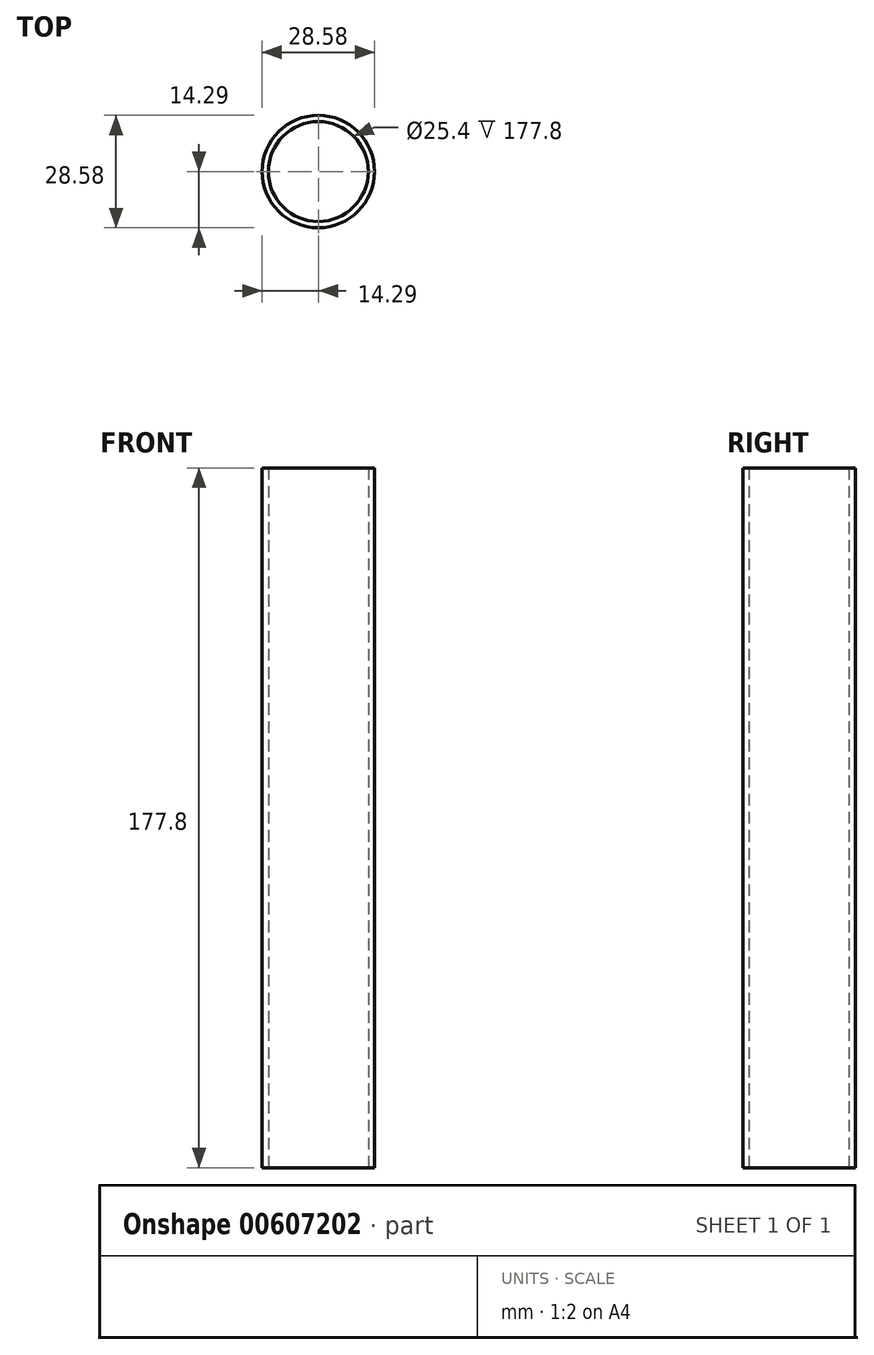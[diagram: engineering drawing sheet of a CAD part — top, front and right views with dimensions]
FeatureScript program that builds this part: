
annotation { "Feature Type Name" : "Feature", "Feature Type Description" : "" }
export const myFeature = defineFeature(function(context is Context, id is Id, definition is map)
    precondition{}
    {
        {
            var Q0;
            Q0=qCreatedBy(makeId("Top.planeOp"),FACE);
            var sketch = newSketch(context, id + "F0", { "sketchPlane" : qUnion([Q0])});
            skLineSegment(sketch, "E0", {"start": v(0, 0) * mm, "end": v(12.7, 0) * mm});
            skCircle(sketch, "E1", {"center": v(0, 0) * mm, "radius": 12.7 * mm});
            skCircle(sketch, "E2.0", {"center": v(0, 0) * mm, "radius": 14.29 * mm});
            skSolve(sketch);
        }
        {
            var Q0;
            Q0=qCreatedBy(makeId("Top.planeOp"),FACE);
            var sketch = newSketch(context, id + "F1", { "sketchPlane" : qUnion([Q0])});
            skSolve(sketch);
        }
        {
            var Q0;
            Q0=qSketchRegion(id+"F1",true);
            var Q1;
            Q1=makeQuery(id+"F0.imprint","IMPRINT",FACE,{"disambiguationData":[TD([[makeQuery(id+"F0.imprint","IMPRINT",EDGE,{"derivedFrom":sQuery(id+"F0.wireOp",EDGE,"E1")}),-1.0]])]});
            extrude(context, id + "F2", {"entities" : qUnion([Q0, Q1]), "depth" : 177.8 * mm, "offsetDistance" : 25.4 * mm});
        }
    });
